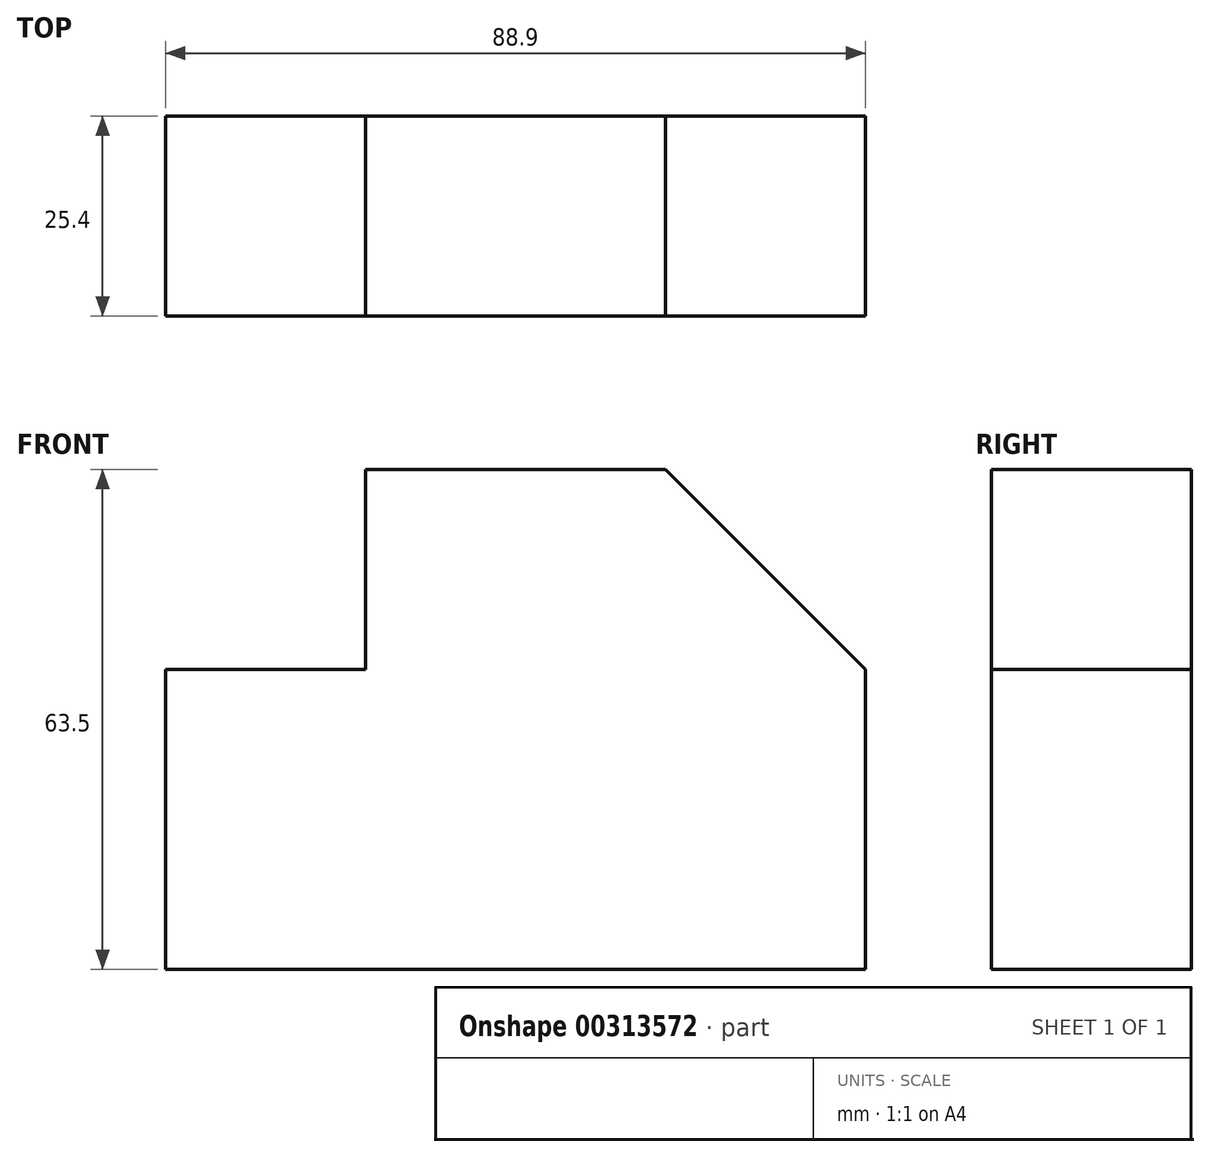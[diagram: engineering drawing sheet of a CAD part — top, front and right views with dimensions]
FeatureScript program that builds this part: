
annotation { "Feature Type Name" : "Feature", "Feature Type Description" : "" }
export const myFeature = defineFeature(function(context is Context, id is Id, definition is map)
    precondition{}
    {
        {
            var Q0;
            Q0=qCreatedBy(makeId("Front.planeOp"),FACE);
            var sketch = newSketch(context, id + "F0", { "sketchPlane" : qUnion([Q0])});
            skLineSegment(sketch, "E0", {"start": v(19.05, 31.75) * mm, "end": v(-19.05, 31.75) * mm});
            skLineSegment(sketch, "E1", {"start": v(-19.05, 31.75) * mm, "end": v(-19.05, 6.35) * mm});
            skLineSegment(sketch, "E2", {"start": v(-19.05, 6.35) * mm, "end": v(-44.45, 6.35) * mm});
            skLineSegment(sketch, "E3", {"start": v(-44.45, 6.35) * mm, "end": v(-44.45, -31.75) * mm});
            skLineSegment(sketch, "E4", {"start": v(-44.45, -31.75) * mm, "end": v(44.45, -31.75) * mm});
            skLineSegment(sketch, "E5", {"start": v(44.45, -31.75) * mm, "end": v(44.45, 6.35) * mm});
            skLineSegment(sketch, "E6", {"start": v(44.45, 6.35) * mm, "end": v(19.05, 31.75) * mm});
            skSolve(sketch);
        }
        {
            var Q0;
            Q0=makeQuery(id+"F0.imprint","IMPRINT",FACE,{"disambiguationData":[TD([[makeQuery(id+"F0.imprint","IMPRINT",EDGE,{"derivedFrom":sQuery(id+"F0.wireOp",EDGE,"E0")}),1.0]])]});
            extrude(context, id + "F1", {"entities" : qUnion([Q0]), "depth" : 25.4 * mm});
        }
    });
